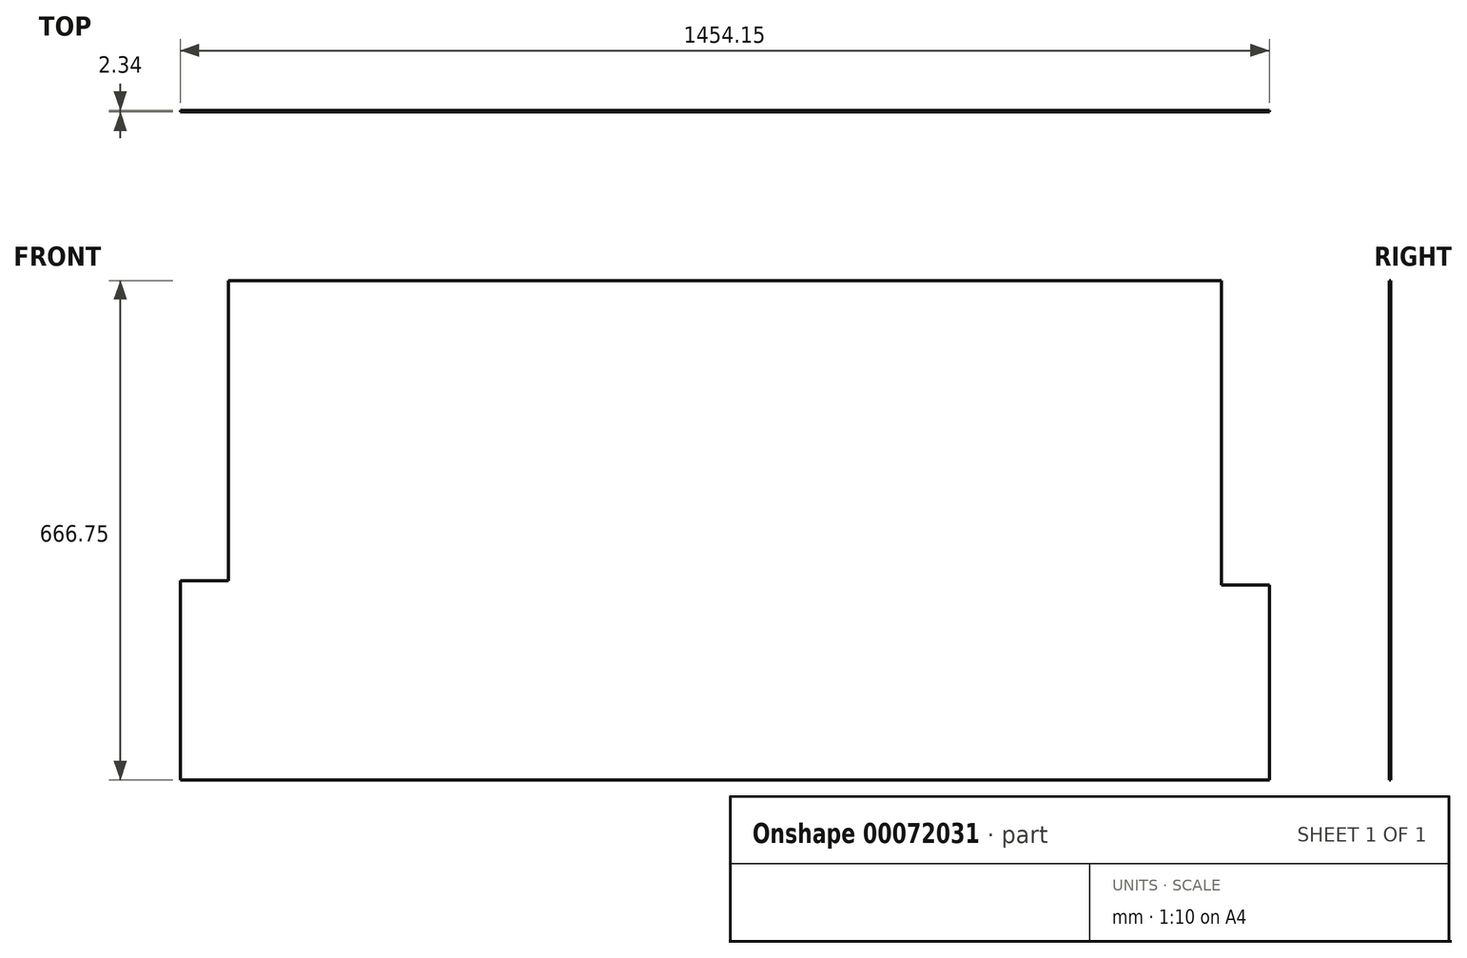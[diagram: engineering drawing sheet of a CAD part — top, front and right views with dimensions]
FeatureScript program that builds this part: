
annotation { "Feature Type Name" : "Feature", "Feature Type Description" : "" }
export const myFeature = defineFeature(function(context is Context, id is Id, definition is map)
    precondition{}
    {
        {
            var Q0;
            Q0=qCreatedBy(makeId("Front.planeOp"),FACE);
            var sketch = newSketch(context, id + "F0", { "sketchPlane" : qUnion([Q0])});
            skLineSegment(sketch, "E0.bottom", {"start": v(0, 0) * mm, "end": v(1326.24, 0) * mm});
            skLineSegment(sketch, "E0.top", {"start": v(-64.26, -666.75) * mm, "end": v(1389.89, -666.75) * mm});
            skLineSegment(sketch, "E0.left", {"start": v(-64.26, -400.81) * mm, "end": v(-64.26, -666.75) * mm});
            skLineSegment(sketch, "E0.right", {"start": v(1389.89, -406.4) * mm, "end": v(1389.89, -666.75) * mm});
            skLineSegment(sketch, "E1.0", {"start": v(1326.24, -406.4) * mm, "end": v(1389.89, -406.4) * mm});
            skLineSegment(sketch, "E2.0", {"start": v(-64.26, -400.81) * mm, "end": v(0, -400.81) * mm});
            skLineSegment(sketch, "E3.0", {"start": v(0, 0) * mm, "end": v(0, -400.81) * mm});
            skLineSegment(sketch, "E4.0", {"start": v(1326.24, 0) * mm, "end": v(1326.24, -406.4) * mm});
            skPoint(sketch, "E5", {"position": v(0, 0) * mm});
            skSolve(sketch);
        }
        {
            var Q0;
            Q0 = qSketchRegion(id + "F0", true);
            extrude(context, id + "F1", {"entities" : qUnion([Q0]), "depth" : 2.34 * mm});
        }
    });
